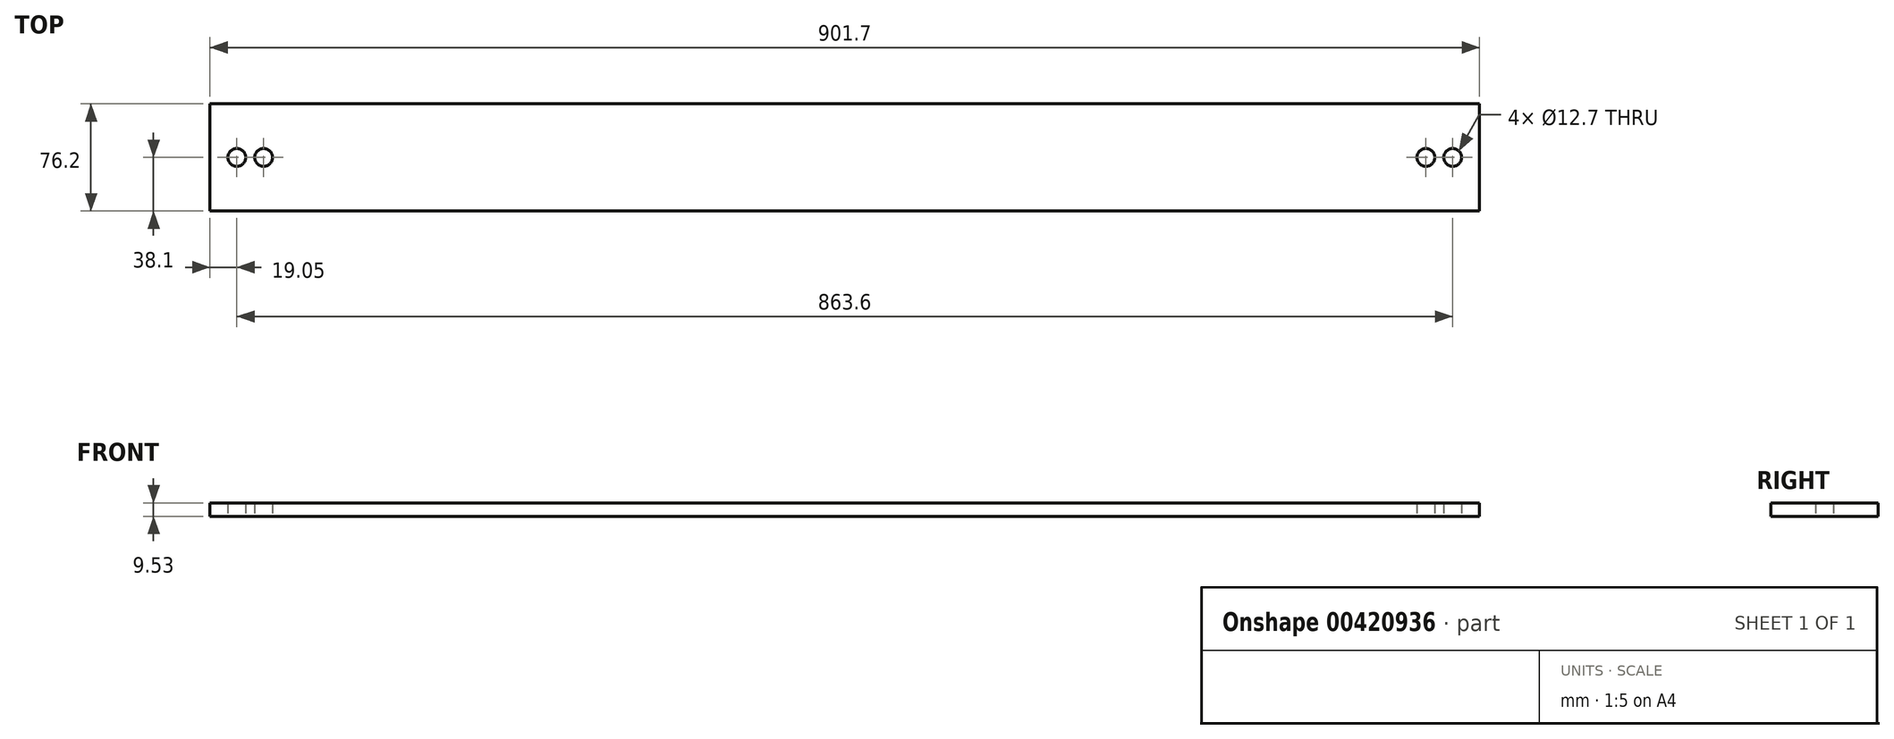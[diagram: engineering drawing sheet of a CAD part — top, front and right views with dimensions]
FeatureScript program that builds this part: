
annotation { "Feature Type Name" : "Feature", "Feature Type Description" : "" }
export const myFeature = defineFeature(function(context is Context, id is Id, definition is map)
    precondition{}
    {
        {
            var Q0;
            Q0=qCreatedBy(makeId("Top.planeOp"),FACE);
            var sketch = newSketch(context, id + "F0", { "sketchPlane" : qUnion([Q0])});
            skLineSegment(sketch, "E0.bottom", {"start": v(0, 0) * mm, "end": v(901.7, 0) * mm});
            skLineSegment(sketch, "E0.top", {"start": v(0, -76.2) * mm, "end": v(901.7, -76.2) * mm});
            skLineSegment(sketch, "E0.left", {"start": v(0, 0) * mm, "end": v(0, -76.2) * mm});
            skLineSegment(sketch, "E0.right", {"start": v(901.7, 0) * mm, "end": v(901.7, -76.2) * mm});
            skCircle(sketch, "E1", {"center": v(19.05, -38.1) * mm, "radius": 6.35 * mm});
            skCircle(sketch, "E2", {"center": v(38.1, -38.1) * mm, "radius": 6.35 * mm});
            skCircle(sketch, "E3", {"center": v(863.6, -38.1) * mm, "radius": 6.35 * mm});
            skCircle(sketch, "E4", {"center": v(882.65, -38.1) * mm, "radius": 6.35 * mm});
            skPoint(sketch, "E5", {"position": v(0, -38.1) * mm});
            skSolve(sketch);
        }
        {
            var Q0;
            Q0=qSketchRegion(id+"F0",true);
            extrude(context, id + "F1", {"entities" : qUnion([Q0]), "depth" : 9.52 * mm});
        }
    });
